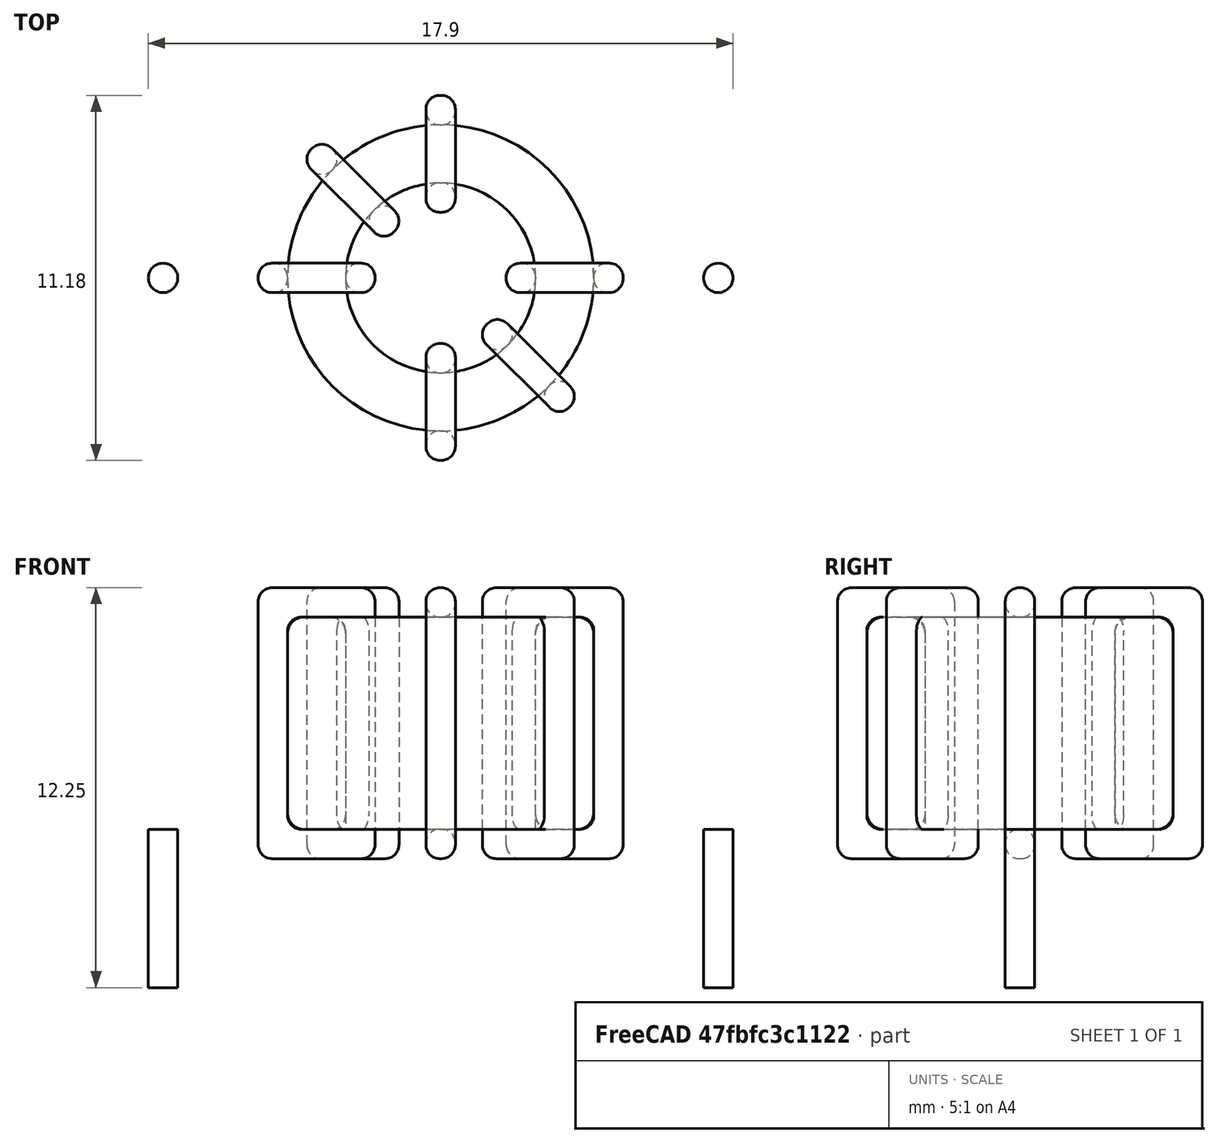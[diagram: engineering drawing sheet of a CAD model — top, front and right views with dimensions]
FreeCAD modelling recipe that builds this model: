
FCSTD DOCUMENT  (FreeCAD 0.16R6703 (Git))
Label: L_Toroid_Horizontal_D11.2mm_P17.00mm_Diameter12-5mm_Amidon-T44
License: All rights reserved
LicenseURL: http://en.wikipedia.org/wiki/All_rights_reserved
objects: Sketcher::SketchObject×6, PartDesign::Pad×6, PartDesign::Fillet×5, Spreadsheet::Sheet×1
note: 23 computed .brp shape members not serialized (recipe doc carries the construction recipe); baked Part::Feature solids carry a one-line shape summary decoded from their .brp

FEATURE [Spreadsheet::Sheet] Spreadsheet  label="dimensions"
  cells = A1=Wx; B1(Wx)=11.176; C1(WW)=5.8166; D1=11.176; A2=Wy; B2(Wy)=11.176; D2=11.176; A3=RM; B3(RMx)=17; C3(RMy)=0; A4=d_wire; B4(d_wire)=0.8999999999999999; A5=H; B5(H)=6.5; A6=offsetx; B6(offsetx)=-2.912
FEATURE [Sketcher::SketchObject] Sketch
  Placement = pos=(0,0,1.4) rot=(0,0,1;0rad)
  expr: Placement.Base.z = 0.5 + Spreadsheet.d_wire
  expr: Constraints[0] = Spreadsheet.Wx / 2 - Spreadsheet.d_wire
  expr: Constraints[4] = Spreadsheet.WW / 2
  expr: Constraints[2] = Spreadsheet.RMy / 2
  expr: Constraints[1] = Spreadsheet.RMx / 2
  sketch-geometry (2):
    g0: Circle CenterX=8.5 CenterY=0 CenterZ=0 NormalX=0 NormalY=0 NormalZ=1 Radius=4.688
    g1: Circle CenterX=8.5 CenterY=0 CenterZ=0 NormalX=0 NormalY=0 NormalZ=1 Radius=2.9083
  constraints (5):
    c: Radius(g0) = 4.688
    c: DistanceX(g-1,g0) = 8.5
    c: DistanceY(g-1,g0) = 0
    c: Coincident(g1,g0)
    c: Radius(g1) = 2.9083
FEATURE [PartDesign::Pad] Pad
  Length = 6.5
  Length2 = 100
  Placement = pos=(0,0,1.4) rot=(0,0,1;0rad)
  Sketch = -> Sketch
  Type = 0
  expr: Length = Spreadsheet.H
FEATURE [Sketcher::SketchObject] Sketch001
  Placement = pos=(0,0,0.95) rot=(0,0,1;0rad)
  expr: Placement.Base.z = 0.5 + Spreadsheet.d_wire * 0.5
  expr: Constraints[4] = Spreadsheet.RMx
  expr: Constraints[2] = Spreadsheet.RMy
  expr: Constraints[1] = Spreadsheet.d_wire / 2
  sketch-geometry (2):
    g0: Circle CenterX=0 CenterY=0 CenterZ=0 NormalX=0 NormalY=0 NormalZ=1 Radius=0.45
    g1: Circle CenterX=17 CenterY=0 CenterZ=0 NormalX=0 NormalY=0 NormalZ=1 Radius=0.45
  constraints (5):
    c: Equal(g0,g1)
    c: Radius(g0) = 0.45
    c: DistanceY(g-1,g1) = 0
    c: Coincident(g0,g-1)
    c: DistanceX(g-1,g1) = 17
FEATURE [PartDesign::Pad] Pad001
  Length = 0.45
  Length2 = 4.4
  Placement = pos=(0,0,0.95) rot=(0,0,1;0rad)
  Reversed = true
  Sketch = -> Sketch001
  Type = 4
  expr: Length2 = 3.5 + Spreadsheet.d_wire
  expr: Length = Spreadsheet.d_wire / 2
FEATURE [PartDesign::Fillet] Fillet
  Base = -> Pad [Edge6,Edge3,Edge2]
  Placement = pos=(0,0,1.4) rot=(0,0,1;0rad)
  Radius = 0.5
FEATURE [Sketcher::SketchObject] Sketch003
  Placement = pos=(8.5,0,0) rot=(1,0,0;1.5708rad)
  expr: Placement.Base.x = Spreadsheet.RMx / 2
  expr: Constraints[49] = Spreadsheet.Wx - Spreadsheet.d_wire * 2
  expr: Constraints[44] = Spreadsheet.d_wire
  expr: Constraints[23] = Spreadsheet.H
  expr: Constraints[22] = Spreadsheet.Wx / 2 - Spreadsheet.d_wire
  expr: Placement.Base.y = Spreadsheet.RMy / 2
  expr: Constraints[21] = (Spreadsheet.Wx - Spreadsheet.WW) / 2 - Spreadsheet.d_wire
  expr: Constraints[19] = Spreadsheet.d_wire
  expr: Constraints[17] = Spreadsheet.d_wire
  expr: Constraints[18] = Spreadsheet.d_wire
  expr: Constraints[16] = Spreadsheet.d_wire
  sketch-geometry (16):
    g0: LineSegment StartX=-2.0083 StartY=0.5 StartZ=0 EndX=-5.588 EndY=0.5 EndZ=0
    g1: LineSegment StartX=-5.588 StartY=0.5 StartZ=0 EndX=-5.588 EndY=8.8 EndZ=0
    g2: LineSegment StartX=-5.588 StartY=8.8 StartZ=0 EndX=-2.0083 EndY=8.8 EndZ=0
    g3: LineSegment StartX=-2.0083 StartY=8.8 StartZ=0 EndX=-2.0083 EndY=0.5 EndZ=0
    g4: LineSegment StartX=-4.688 StartY=7.9 StartZ=0 EndX=-2.9083 EndY=7.9 EndZ=0
    g5: LineSegment StartX=-2.9083 StartY=7.9 StartZ=0 EndX=-2.9083 EndY=1.4 EndZ=0
    g6: LineSegment StartX=-2.9083 StartY=1.4 StartZ=0 EndX=-4.688 EndY=1.4 EndZ=0
    g7: LineSegment StartX=-4.688 StartY=1.4 StartZ=0 EndX=-4.688 EndY=7.9 EndZ=0
    g8: LineSegment StartX=2.0083 StartY=8.8 StartZ=0 EndX=5.588 EndY=8.8 EndZ=0
    g9: LineSegment StartX=5.588 StartY=8.8 StartZ=0 EndX=5.588 EndY=0.5 EndZ=0
    g10: LineSegment StartX=5.588 StartY=0.5 StartZ=0 EndX=2.0083 EndY=0.5 EndZ=0
    g11: LineSegment StartX=2.0083 StartY=0.5 StartZ=0 EndX=2.0083 EndY=8.8 EndZ=0
    g12: LineSegment StartX=2.9083 StartY=7.9 StartZ=0 EndX=4.688 EndY=7.9 EndZ=0
    g13: LineSegment StartX=4.688 StartY=7.9 StartZ=0 EndX=4.688 EndY=1.4 EndZ=0
    g14: LineSegment StartX=4.688 StartY=1.4 StartZ=0 EndX=2.9083 EndY=1.4 EndZ=0
    g15: LineSegment StartX=2.9083 StartY=1.4 StartZ=0 EndX=2.9083 EndY=7.9 EndZ=0
  constraints (50):
    c: Horizontal(g0)
    c: Coincident(g1,g0)
    c: Vertical(g1)
    c: Coincident(g2,g1)
    c: Horizontal(g2)
    c: Coincident(g3,g2)
    c: Coincident(g3,g0)
    c: Vertical(g3)
    c: Coincident(g4,g5)
    c: Coincident(g5,g6)
    c: Coincident(g6,g7)
    c: Coincident(g7,g4)
    c: Horizontal(g4)
    c: Horizontal(g6)
    c: Vertical(g5)
    c: Vertical(g7)
    c: DistanceX(g1,g4) = 0.9
    c: DistanceY(g4,g1) = 0.9
    c: DistanceX(g5,g0) = 0.9
    c: DistanceY(g0,g5) = 0.9
    c: DistanceY(g-1,g0) = 0.5
    c: DistanceX(g6,g6) = 1.7797
    c: DistanceX(g6,g-1) = 4.688
    c: DistanceY(g7,g7) = 6.5
    c: Coincident(g8,g9)
    c: Coincident(g9,g10)
    c: Coincident(g10,g11)
    c: Coincident(g11,g8)
    c: Horizontal(g8)
    c: Horizontal(g10)
    c: Vertical(g9)
    c: Vertical(g11)
    c: Coincident(g12,g13)
    c: Coincident(g13,g14)
    c: Coincident(g14,g15)
    c: Coincident(g15,g12)
    c: Horizontal(g12)
    c: Horizontal(g14)
    c: Vertical(g13)
    c: Vertical(g15)
    c: DistanceY(g8,g2) = 0
    c: DistanceY(g10,g0) = 0
    c: DistanceY(g14,g5) = 0
    c: DistanceY(g12,g4) = 0
    c: DistanceX(g8,g12) = 0.9
    c: Equal(g8,g2)
    c: Equal(g12,g4)
    c: Equal(g9,g1)
    c: Equal(g13,g7)
    c: DistanceX(g4,g12) = 9.376
FEATURE [PartDesign::Pad] Pad002
  Length = 0.9
  Length2 = 100
  Midplane = true
  Placement = pos=(8.5,0,0) rot=(1,0,0;1.5708rad)
  Sketch = -> Sketch003
  Type = 0
  expr: Length = Spreadsheet.d_wire
FEATURE [PartDesign::Fillet] Fillet001
  Base = -> Pad002 [Edge38,Edge41,Edge42,Edge43,Edge29,Edge32,Edge33,Edge34,Edge25,Edge35,Edge36,Edge13,Edge14,Edge15,Edge16,Edge17,Edge18,Edge19,Edge1,Edge2,Edge3,Edge4,Edge5,Edge6,Edge7,Edge37,Edge39,Edge40,Edge20,Edge23,Edge24,Edge21,Edge22,Edge8,Edge9,Edge10,Edge11,Edge12,Edge26,Edge27,+8 more]
  Placement = pos=(8.5,0,0) rot=(1,0,0;1.5708rad)
  Radius = 0.423
  expr: Radius = Spreadsheet.d_wire * 0.47
FEATURE [Sketcher::SketchObject] Sketch004
  Placement = pos=(8.5,0,0) rot=(0.862856,0.357407,0.357407;1.71777rad)
  expr: Placement.Base.x = Spreadsheet.RMx / 2
  expr: Constraints[49] = Spreadsheet.Wx - 2 * Spreadsheet.d_wire
  expr: Constraints[44] = Spreadsheet.d_wire
  expr: Constraints[23] = Spreadsheet.H
  expr: Constraints[22] = Spreadsheet.Wx / 2 - Spreadsheet.d_wire
  expr: Placement.Base.y = Spreadsheet.RMy / 2
  expr: Constraints[21] = (Spreadsheet.Wx - Spreadsheet.WW) / 2 - Spreadsheet.d_wire
  expr: Constraints[19] = Spreadsheet.d_wire
  expr: Constraints[17] = Spreadsheet.d_wire
  expr: Constraints[18] = Spreadsheet.d_wire
  expr: Constraints[16] = Spreadsheet.d_wire
  sketch-geometry (16):
    g0: LineSegment StartX=-2.0083 StartY=0.5 StartZ=0 EndX=-5.588 EndY=0.5 EndZ=0
    g1: LineSegment StartX=-5.588 StartY=0.5 StartZ=0 EndX=-5.588 EndY=8.8 EndZ=0
    g2: LineSegment StartX=-5.588 StartY=8.8 StartZ=0 EndX=-2.0083 EndY=8.8 EndZ=0
    g3: LineSegment StartX=-2.0083 StartY=8.8 StartZ=0 EndX=-2.0083 EndY=0.5 EndZ=0
    g4: LineSegment StartX=-4.688 StartY=7.9 StartZ=0 EndX=-2.9083 EndY=7.9 EndZ=0
    g5: LineSegment StartX=-2.9083 StartY=7.9 StartZ=0 EndX=-2.9083 EndY=1.4 EndZ=0
    g6: LineSegment StartX=-2.9083 StartY=1.4 StartZ=0 EndX=-4.688 EndY=1.4 EndZ=0
    g7: LineSegment StartX=-4.688 StartY=1.4 StartZ=0 EndX=-4.688 EndY=7.9 EndZ=0
    g8: LineSegment StartX=2.0083 StartY=8.8 StartZ=0 EndX=5.588 EndY=8.8 EndZ=0
    g9: LineSegment StartX=5.588 StartY=8.8 StartZ=0 EndX=5.588 EndY=0.5 EndZ=0
    g10: LineSegment StartX=5.588 StartY=0.5 StartZ=0 EndX=2.0083 EndY=0.5 EndZ=0
    g11: LineSegment StartX=2.0083 StartY=0.5 StartZ=0 EndX=2.0083 EndY=8.8 EndZ=0
    g12: LineSegment StartX=2.9083 StartY=7.9 StartZ=0 EndX=4.688 EndY=7.9 EndZ=0
    g13: LineSegment StartX=4.688 StartY=7.9 StartZ=0 EndX=4.688 EndY=1.4 EndZ=0
    g14: LineSegment StartX=4.688 StartY=1.4 StartZ=0 EndX=2.9083 EndY=1.4 EndZ=0
    g15: LineSegment StartX=2.9083 StartY=1.4 StartZ=0 EndX=2.9083 EndY=7.9 EndZ=0
  constraints (50):
    c: Horizontal(g0)
    c: Coincident(g1,g0)
    c: Vertical(g1)
    c: Coincident(g2,g1)
    c: Horizontal(g2)
    c: Coincident(g3,g2)
    c: Coincident(g3,g0)
    c: Vertical(g3)
    c: Coincident(g4,g5)
    c: Coincident(g5,g6)
    c: Coincident(g6,g7)
    c: Coincident(g7,g4)
    c: Horizontal(g4)
    c: Horizontal(g6)
    c: Vertical(g5)
    c: Vertical(g7)
    c: DistanceX(g1,g4) = 0.9
    c: DistanceY(g4,g1) = 0.9
    c: DistanceX(g5,g0) = 0.9
    c: DistanceY(g0,g5) = 0.9
    c: DistanceY(g-1,g0) = 0.5
    c: DistanceX(g6,g6) = 1.7797
    c: DistanceX(g6,g-1) = 4.688
    c: DistanceY(g7,g7) = 6.5
    c: Coincident(g8,g9)
    c: Coincident(g9,g10)
    c: Coincident(g10,g11)
    c: Coincident(g11,g8)
    c: Horizontal(g8)
    c: Horizontal(g10)
    c: Vertical(g9)
    c: Vertical(g11)
    c: Coincident(g12,g13)
    c: Coincident(g13,g14)
    c: Coincident(g14,g15)
    c: Coincident(g15,g12)
    c: Horizontal(g12)
    c: Horizontal(g14)
    c: Vertical(g13)
    c: Vertical(g15)
    c: DistanceY(g8,g2) = 0
    c: DistanceY(g10,g0) = 0
    c: DistanceY(g14,g5) = 0
    c: DistanceY(g12,g4) = 0
    c: DistanceX(g8,g12) = 0.9
    c: Equal(g8,g2)
    c: Equal(g12,g4)
    c: Equal(g9,g1)
    c: Equal(g13,g7)
    c: DistanceX(g4,g12) = 9.376
FEATURE [PartDesign::Pad] Pad003
  Length = 0.9
  Length2 = 100
  Midplane = true
  Placement = pos=(8.5,0,0) rot=(0.862856,0.357407,0.357407;1.71777rad)
  Sketch = -> Sketch004
  Type = 0
  expr: Length = Spreadsheet.d_wire
FEATURE [PartDesign::Fillet] Fillet002
  Base = -> Pad003 [Edge38,Edge41,Edge42,Edge43,Edge29,Edge32,Edge33,Edge34,Edge25,Edge35,Edge36,Edge13,Edge14,Edge15,Edge16,Edge17,Edge18,Edge19,Edge1,Edge2,Edge3,Edge4,Edge5,Edge6,Edge7,Edge37,Edge39,Edge40,Edge20,Edge23,Edge24,Edge21,Edge22,Edge8,Edge9,Edge10,Edge11,Edge12,Edge26,Edge27,+8 more]
  Placement = pos=(8.5,0,0) rot=(0.862856,0.357407,0.357407;1.71777rad)
  Radius = 0.423
  expr: Radius = Spreadsheet.d_wire * 0.47
FEATURE [Sketcher::SketchObject] Sketch005
  Placement = pos=(8.5,0,0) rot=(0.862856,-0.357407,-0.357407;1.71777rad)
  expr: Placement.Base.x = Spreadsheet.RMx / 2
  expr: Constraints[49] = Spreadsheet.Wx - 2 * Spreadsheet.d_wire
  expr: Constraints[44] = Spreadsheet.d_wire
  expr: Constraints[23] = Spreadsheet.H
  expr: Constraints[22] = Spreadsheet.Wx / 2 - Spreadsheet.d_wire
  expr: Placement.Base.y = Spreadsheet.RMy / 2
  expr: Constraints[21] = (Spreadsheet.Wx - Spreadsheet.WW) / 2 - Spreadsheet.d_wire
  expr: Constraints[19] = Spreadsheet.d_wire
  expr: Constraints[17] = Spreadsheet.d_wire
  expr: Constraints[18] = Spreadsheet.d_wire
  expr: Constraints[16] = Spreadsheet.d_wire
  sketch-geometry (16):
    g0: LineSegment StartX=-2.0083 StartY=0.5 StartZ=0 EndX=-5.588 EndY=0.5 EndZ=0
    g1: LineSegment StartX=-5.588 StartY=0.5 StartZ=0 EndX=-5.588 EndY=8.8 EndZ=0
    g2: LineSegment StartX=-5.588 StartY=8.8 StartZ=0 EndX=-2.0083 EndY=8.8 EndZ=0
    g3: LineSegment StartX=-2.0083 StartY=8.8 StartZ=0 EndX=-2.0083 EndY=0.5 EndZ=0
    g4: LineSegment StartX=-4.688 StartY=7.9 StartZ=0 EndX=-2.9083 EndY=7.9 EndZ=0
    g5: LineSegment StartX=-2.9083 StartY=7.9 StartZ=0 EndX=-2.9083 EndY=1.4 EndZ=0
    g6: LineSegment StartX=-2.9083 StartY=1.4 StartZ=0 EndX=-4.688 EndY=1.4 EndZ=0
    g7: LineSegment StartX=-4.688 StartY=1.4 StartZ=0 EndX=-4.688 EndY=7.9 EndZ=0
    g8: LineSegment StartX=2.0083 StartY=8.8 StartZ=0 EndX=5.588 EndY=8.8 EndZ=0
    g9: LineSegment StartX=5.588 StartY=8.8 StartZ=0 EndX=5.588 EndY=0.5 EndZ=0
    g10: LineSegment StartX=5.588 StartY=0.5 StartZ=0 EndX=2.0083 EndY=0.5 EndZ=0
    g11: LineSegment StartX=2.0083 StartY=0.5 StartZ=0 EndX=2.0083 EndY=8.8 EndZ=0
    g12: LineSegment StartX=2.9083 StartY=7.9 StartZ=0 EndX=4.688 EndY=7.9 EndZ=0
    g13: LineSegment StartX=4.688 StartY=7.9 StartZ=0 EndX=4.688 EndY=1.4 EndZ=0
    g14: LineSegment StartX=4.688 StartY=1.4 StartZ=0 EndX=2.9083 EndY=1.4 EndZ=0
    g15: LineSegment StartX=2.9083 StartY=1.4 StartZ=0 EndX=2.9083 EndY=7.9 EndZ=0
  constraints (50):
    c: Horizontal(g0)
    c: Coincident(g1,g0)
    c: Vertical(g1)
    c: Coincident(g2,g1)
    c: Horizontal(g2)
    c: Coincident(g3,g2)
    c: Coincident(g3,g0)
    c: Vertical(g3)
    c: Coincident(g4,g5)
    c: Coincident(g5,g6)
    c: Coincident(g6,g7)
    c: Coincident(g7,g4)
    c: Horizontal(g4)
    c: Horizontal(g6)
    c: Vertical(g5)
    c: Vertical(g7)
    c: DistanceX(g1,g4) = 0.9
    c: DistanceY(g4,g1) = 0.9
    c: DistanceX(g5,g0) = 0.9
    c: DistanceY(g0,g5) = 0.9
    c: DistanceY(g-1,g0) = 0.5
    c: DistanceX(g6,g6) = 1.7797
    c: DistanceX(g6,g-1) = 4.688
    c: DistanceY(g7,g7) = 6.5
    c: Coincident(g8,g9)
    c: Coincident(g9,g10)
    c: Coincident(g10,g11)
    c: Coincident(g11,g8)
    c: Horizontal(g8)
    c: Horizontal(g10)
    c: Vertical(g9)
    c: Vertical(g11)
    c: Coincident(g12,g13)
    c: Coincident(g13,g14)
    c: Coincident(g14,g15)
    c: Coincident(g15,g12)
    c: Horizontal(g12)
    c: Horizontal(g14)
    c: Vertical(g13)
    c: Vertical(g15)
    c: DistanceY(g8,g2) = 0
    c: DistanceY(g10,g0) = 0
    c: DistanceY(g14,g5) = 0
    c: DistanceY(g12,g4) = 0
    c: DistanceX(g8,g12) = 0.9
    c: Equal(g8,g2)
    c: Equal(g12,g4)
    c: Equal(g9,g1)
    c: Equal(g13,g7)
    c: DistanceX(g4,g12) = 9.376
FEATURE [PartDesign::Pad] Pad004
  Length = 0.9
  Length2 = 100
  Midplane = true
  Placement = pos=(8.5,0,0) rot=(0.862856,-0.357407,-0.357407;1.71777rad)
  Sketch = -> Sketch005
  Type = 0
  expr: Length = Spreadsheet.d_wire
FEATURE [PartDesign::Fillet] Fillet003
  Base = -> Pad004 [Edge38,Edge41,Edge42,Edge43,Edge29,Edge32,Edge33,Edge34,Edge25,Edge35,Edge36,Edge13,Edge14,Edge15,Edge16,Edge17,Edge18,Edge19,Edge1,Edge2,Edge3,Edge4,Edge5,Edge6,Edge7,Edge37,Edge39,Edge40,Edge20,Edge23,Edge24,Edge21,Edge22,Edge8,Edge9,Edge10,Edge11,Edge12,Edge26,Edge27,+8 more]
  Placement = pos=(8.5,0,0) rot=(0.862856,-0.357407,-0.357407;1.71777rad)
  Radius = 0.423
  expr: Radius = Spreadsheet.d_wire * 0.47
FEATURE [Sketcher::SketchObject] Sketch006
  Placement = pos=(8.5,0,0) rot=(0.57735,0.57735,0.57735;2.0944rad)
  expr: Placement.Base.x = Spreadsheet.RMx / 2
  expr: Constraints[49] = Spreadsheet.Wx - Spreadsheet.d_wire * 2
  expr: Constraints[44] = Spreadsheet.d_wire
  expr: Constraints[23] = Spreadsheet.H
  expr: Constraints[22] = Spreadsheet.Wx / 2 - Spreadsheet.d_wire
  expr: Placement.Base.y = Spreadsheet.RMy / 2
  expr: Constraints[21] = (Spreadsheet.Wx - Spreadsheet.WW) / 2 - Spreadsheet.d_wire
  expr: Constraints[19] = Spreadsheet.d_wire
  expr: Constraints[17] = Spreadsheet.d_wire
  expr: Constraints[18] = Spreadsheet.d_wire
  expr: Constraints[16] = Spreadsheet.d_wire
  sketch-geometry (16):
    g0: LineSegment StartX=-2.0083 StartY=0.5 StartZ=0 EndX=-5.588 EndY=0.5 EndZ=0
    g1: LineSegment StartX=-5.588 StartY=0.5 StartZ=0 EndX=-5.588 EndY=8.8 EndZ=0
    g2: LineSegment StartX=-5.588 StartY=8.8 StartZ=0 EndX=-2.0083 EndY=8.8 EndZ=0
    g3: LineSegment StartX=-2.0083 StartY=8.8 StartZ=0 EndX=-2.0083 EndY=0.5 EndZ=0
    g4: LineSegment StartX=-4.688 StartY=7.9 StartZ=0 EndX=-2.9083 EndY=7.9 EndZ=0
    g5: LineSegment StartX=-2.9083 StartY=7.9 StartZ=0 EndX=-2.9083 EndY=1.4 EndZ=0
    g6: LineSegment StartX=-2.9083 StartY=1.4 StartZ=0 EndX=-4.688 EndY=1.4 EndZ=0
    g7: LineSegment StartX=-4.688 StartY=1.4 StartZ=0 EndX=-4.688 EndY=7.9 EndZ=0
    g8: LineSegment StartX=2.0083 StartY=8.8 StartZ=0 EndX=5.588 EndY=8.8 EndZ=0
    g9: LineSegment StartX=5.588 StartY=8.8 StartZ=0 EndX=5.588 EndY=0.5 EndZ=0
    g10: LineSegment StartX=5.588 StartY=0.5 StartZ=0 EndX=2.0083 EndY=0.5 EndZ=0
    g11: LineSegment StartX=2.0083 StartY=0.5 StartZ=0 EndX=2.0083 EndY=8.8 EndZ=0
    g12: LineSegment StartX=2.9083 StartY=7.9 StartZ=0 EndX=4.688 EndY=7.9 EndZ=0
    g13: LineSegment StartX=4.688 StartY=7.9 StartZ=0 EndX=4.688 EndY=1.4 EndZ=0
    g14: LineSegment StartX=4.688 StartY=1.4 StartZ=0 EndX=2.9083 EndY=1.4 EndZ=0
    g15: LineSegment StartX=2.9083 StartY=1.4 StartZ=0 EndX=2.9083 EndY=7.9 EndZ=0
  constraints (50):
    c: Horizontal(g0)
    c: Coincident(g1,g0)
    c: Vertical(g1)
    c: Coincident(g2,g1)
    c: Horizontal(g2)
    c: Coincident(g3,g2)
    c: Coincident(g3,g0)
    c: Vertical(g3)
    c: Coincident(g4,g5)
    c: Coincident(g5,g6)
    c: Coincident(g6,g7)
    c: Coincident(g7,g4)
    c: Horizontal(g4)
    c: Horizontal(g6)
    c: Vertical(g5)
    c: Vertical(g7)
    c: DistanceX(g1,g4) = 0.9
    c: DistanceY(g4,g1) = 0.9
    c: DistanceX(g5,g0) = 0.9
    c: DistanceY(g0,g5) = 0.9
    c: DistanceY(g-1,g0) = 0.5
    c: DistanceX(g6,g6) = 1.7797
    c: DistanceX(g6,g-1) = 4.688
    c: DistanceY(g7,g7) = 6.5
    c: Coincident(g8,g9)
    c: Coincident(g9,g10)
    c: Coincident(g10,g11)
    c: Coincident(g11,g8)
    c: Horizontal(g8)
    c: Horizontal(g10)
    c: Vertical(g9)
    c: Vertical(g11)
    c: Coincident(g12,g13)
    c: Coincident(g13,g14)
    c: Coincident(g14,g15)
    c: Coincident(g15,g12)
    c: Horizontal(g12)
    c: Horizontal(g14)
    c: Vertical(g13)
    c: Vertical(g15)
    c: DistanceY(g8,g2) = 0
    c: DistanceY(g10,g0) = 0
    c: DistanceY(g14,g5) = 0
    c: DistanceY(g12,g4) = 0
    c: DistanceX(g8,g12) = 0.9
    c: Equal(g8,g2)
    c: Equal(g12,g4)
    c: Equal(g9,g1)
    c: Equal(g13,g7)
    c: DistanceX(g4,g12) = 9.376
FEATURE [PartDesign::Pad] Pad005
  Length = 0.9
  Length2 = 100
  Midplane = true
  Placement = pos=(8.5,0,0) rot=(0.57735,0.57735,0.57735;2.0944rad)
  Sketch = -> Sketch006
  Type = 0
  expr: Length = Spreadsheet.d_wire
FEATURE [PartDesign::Fillet] Fillet004
  Base = -> Pad005 [Edge38,Edge41,Edge42,Edge43,Edge29,Edge32,Edge33,Edge34,Edge25,Edge35,Edge36,Edge13,Edge14,Edge15,Edge16,Edge17,Edge18,Edge19,Edge1,Edge2,Edge3,Edge4,Edge5,Edge6,Edge7,Edge37,Edge39,Edge40,Edge20,Edge23,Edge24,Edge21,Edge22,Edge8,Edge9,Edge10,Edge11,Edge12,Edge26,Edge27,+8 more]
  Placement = pos=(8.5,0,0) rot=(0.57735,0.57735,0.57735;2.0944rad)
  Radius = 0.423
  expr: Radius = Spreadsheet.d_wire * 0.47
